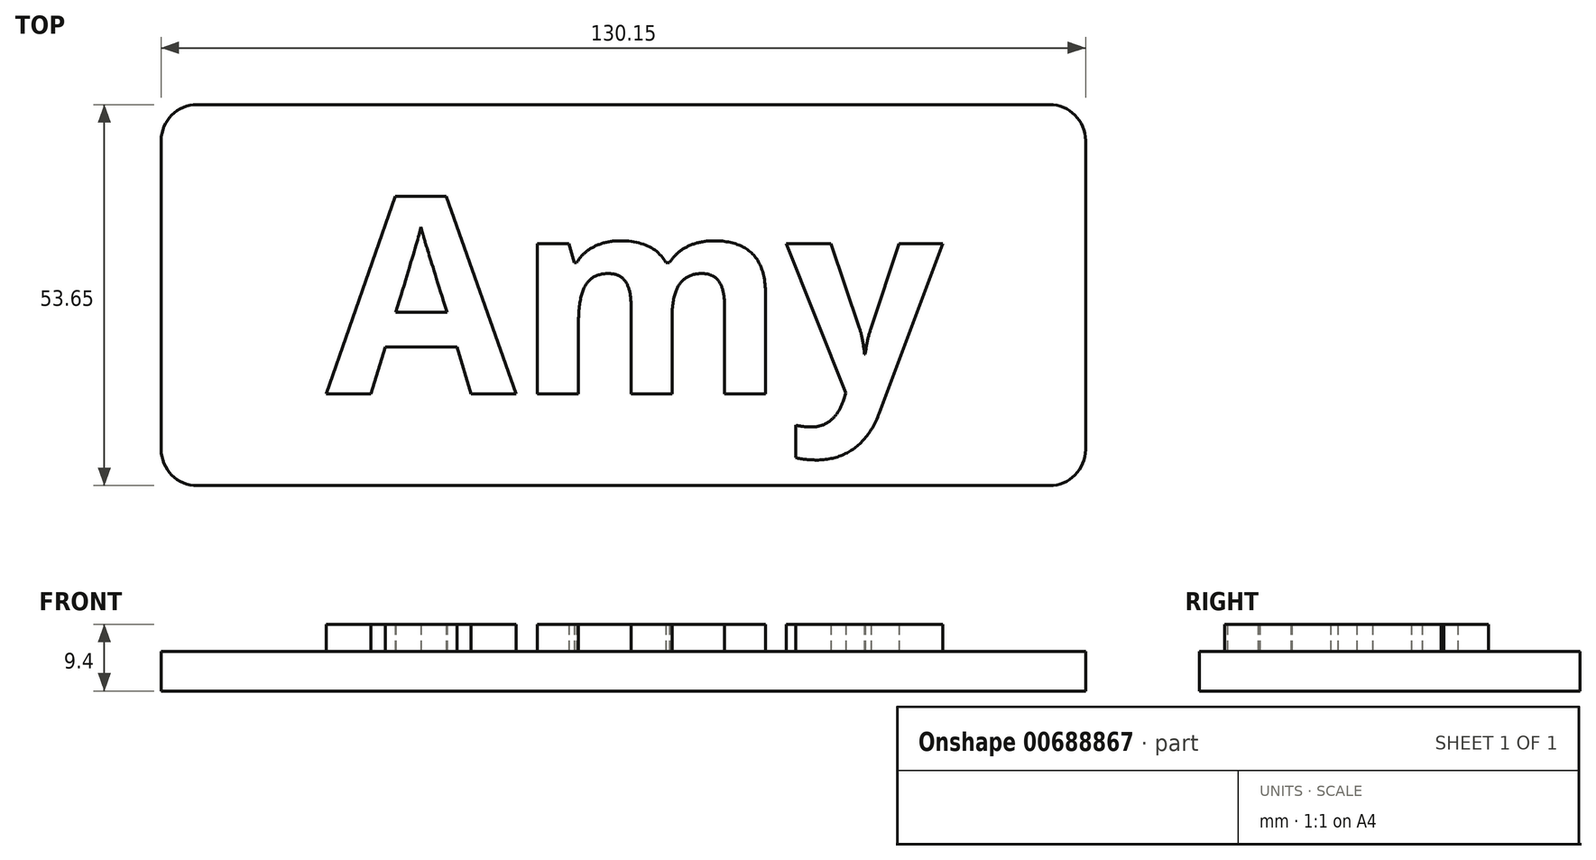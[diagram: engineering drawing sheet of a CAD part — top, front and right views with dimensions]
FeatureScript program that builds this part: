
annotation { "Feature Type Name" : "Feature", "Feature Type Description" : "" }
export const myFeature = defineFeature(function(context is Context, id is Id, definition is map)
    precondition{}
    {
        {
            var Q0;
            Q0=qCreatedBy(makeId("Top.planeOp"),FACE);
            var sketch = newSketch(context, id + "F0", { "sketchPlane" : qUnion([Q0])});
            skLineSegment(sketch, "E0.bottom", {"start": v(-65.38, 31.7) * mm, "end": v(64.77, 31.7) * mm});
            skLineSegment(sketch, "E0.top", {"start": v(-65.38, -21.95) * mm, "end": v(64.77, -21.95) * mm});
            skLineSegment(sketch, "E0.left", {"start": v(-65.38, 31.7) * mm, "end": v(-65.38, -21.95) * mm});
            skLineSegment(sketch, "E0.right", {"start": v(64.77, 31.7) * mm, "end": v(64.77, -21.95) * mm});
            skLineSegment(sketch, "E1.bottom", {"start": v(111.4, -71.93) * mm, "end": v(111.7, -71.93) * mm});
            skLineSegment(sketch, "E1.top", {"start": v(111.4, -78.94) * mm, "end": v(111.7, -78.94) * mm});
            skLineSegment(sketch, "E1.left", {"start": v(111.4, -71.93) * mm, "end": v(111.4, -78.94) * mm});
            skLineSegment(sketch, "E1.right", {"start": v(111.7, -71.93) * mm, "end": v(111.7, -78.94) * mm});
            skSolve(sketch);
        }
        {
            var Q0;
            Q0=makeQuery(id+"F0.imprint","IMPRINT",FACE,{"disambiguationData":[TD([[makeQuery(id+"F0.imprint","IMPRINT",EDGE,{"derivedFrom":sQuery(id+"F0.wireOp",EDGE,"E0.bottom")}),-1.0]])]});
            extrude(context, id + "F1", {"entities" : qUnion([Q0]), "depth" : 5.6 * mm, "offsetDistance" : 25.4 * mm});
        }
        {
            var Q0;
            Q0=makeQuery(id+"F1.opExtrude","SWEPT_EDGE",EDGE,{"disambiguationData":[OSD([sQuery(id+"F0.wireOp",EDGE,"E0.top"),sQuery(id+"F0.wireOp",EDGE,"E0.right")])]});
            fillet(context, id + "F2", {"entities" : qUnion([Q0]), "radius" : 5.08 * mm, "tangentPropagation" : true, "allowEdgeOverflow" : false});
        }
        {
            var Q0;
            Q0=makeQuery(id+"F1.opExtrude","SWEPT_EDGE",EDGE,{"disambiguationData":[OSD([sQuery(id+"F0.wireOp",EDGE,"E0.top"),sQuery(id+"F0.wireOp",EDGE,"E0.left")])]});
            fillet(context, id + "F3", {"entities" : qUnion([Q0]), "radius" : 5.08 * mm, "tangentPropagation" : true, "allowEdgeOverflow" : false});
        }
        {
            var Q0;
            Q0=makeQuery(id+"F1.opExtrude","SWEPT_EDGE",EDGE,{"disambiguationData":[OSD([sQuery(id+"F0.wireOp",EDGE,"E0.bottom"),sQuery(id+"F0.wireOp",EDGE,"E0.left")])]});
            fillet(context, id + "F4", {"entities" : qUnion([Q0]), "radius" : 5.08 * mm, "tangentPropagation" : true, "allowEdgeOverflow" : false});
        }
        {
            var Q0;
            Q0=makeQuery(id+"F1.opExtrude","SWEPT_EDGE",EDGE,{"disambiguationData":[OSD([sQuery(id+"F0.wireOp",EDGE,"E0.bottom"),sQuery(id+"F0.wireOp",EDGE,"E0.right")])]});
            fillet(context, id + "F5", {"entities" : qUnion([Q0]), "radius" : 5.08 * mm, "tangentPropagation" : true, "allowEdgeOverflow" : false});
        }
        {
            var Q0;
            Q0=makeQuery(id+"F1.opExtrude","CAP_FACE",FACE,{"disambiguationData":[OSD([sQuery(id+"F0.wireOp",EDGE,"E0.bottom"),sQuery(id+"F0.wireOp",EDGE,"E0.top"),sQuery(id+"F0.wireOp",EDGE,"E0.left"),sQuery(id+"F0.wireOp",EDGE,"E0.right")])],"isStart":false});
            var sketch = newSketch(context, id + "F6", { "sketchPlane" : qUnion([Q0])});
            skText(sketch, "E2", { "text": "Amy", "fontName": "OpenSans-Bold.ttf"});
            const initialGuessF6  = {"E2": [-0.04216, -0.00903, 1, 0, 0.0279]};
            skSetInitialGuess(sketch, initialGuessF6);
            skSolve(sketch);
        }
        {
            var Q0;
            Q0 = qSketchRegion(id + "F6", true);
            extrude(context, id + "F7", {"entities" : qUnion([Q0]), "operationType" : NewBodyOperationType.ADD, "depth" : 3.8 * mm, "offsetDistance" : 25.4 * mm});
        }
    });
